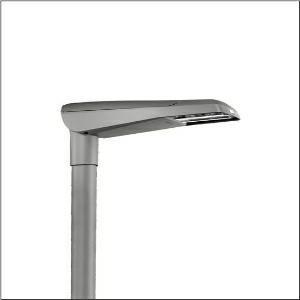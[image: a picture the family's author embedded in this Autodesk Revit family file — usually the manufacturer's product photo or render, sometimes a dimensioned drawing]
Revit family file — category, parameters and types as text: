
# Revit family: streetlight_sl_11_iq_micro___st1_2a_5xc1a51e08ce_3341
name_source: partatom
category: Lighting Fixtures
units: mm (PartAtom-declared; Revit-internal decimal feet)

## family parameters
Cut with Voids When Loaded = No
Host = Face
Light Source = No
Part Type = Normal
Room Calculation Point = No
Round Connector Dimension = Use Diameter
Shared = No

## types (1)
- --- (1 x LED, 1880 lm, 12.6 W, 3000K)
    Apparent Load = 13 VA
    CIE Flux Codes = 33 71 96 100 100
    Color Rendering = 70
    Color Temperature = 3000K
    Default Elevation = 1800 mm
    Description = Streetlight SL 11 iQ micro, mast luminaire, primary light control with 3 zone facetted reflector, of plastic, silver coated, highly specular, primary optical cover: cover, of PMMA, transparent, light distribution: ST1.2a, light emission: direct distribution, primary light characteristic: asymmetric, installation type: post-top, side-entry, lamps: LED, High Power LED, rated values: 1.880lm | 12,6W | 149,2lm/W (begin service life); end service life: 1.880lm | 12,9W; at 50% lumin. flux: 940lm | 6,8W | 138,2lm/W, colour temperature: 3000K, colour rendering: CRI > 70, light colour: 730, light setting 1 begin service life: 100% | 1.880lm | 12,6W | 149,2lm/W | 3.000K, light setting 1 end service life: 12,9W, further light settings possible, control: optimised constant luminous flux control (CLO 2.0), Desk-Remote (wireless, voltage-free reading and setting of iQ features in the workshop via application-optimized NFC function/RFID function), Light-Fading, Smart-Wire, Night-Set, Lumen-Switch, Temp-Guard, Auto-Match, with cable H07RN-F 5x 1.5mm², mains connection: 230..240V, AC, 50/60Hz, connection cable pre-assembled, cable length: 5,5m, luminaire housing, of diecast aluminium, powder-coated, Siteco® metallic grey (DB 702S), please order mast flange separately, inclination adjustable without tools: 0°, 5°, 10°, 15° (post-top) | 0°, -5°, -10°, -15° (side-entry), sealing non-destructively replaceable, multi-level sealing system, length: 600mm, width: 174mm, height: 116mm, mast flange for spigot size: 42mm (side-entry): 5XC10008XM4, 60/48mm (side-entry/post-top): 5XC10108XM2, 76/60mm (side-entry/post-top): 5XC10108XM1, equipment: standard, protection rating (complete): IP66, insulation class (complete): insulation class II (safety insulation), certification: CE, ENEC, ENEC+, VDE, impact resistance: IK10, permissible operating ambient temperature for outdoor applications: -25..+50°C, standard-compliant lighting for roads and squares, Environmental Product Declaration (EPD) tested and certified by an independent institute, packaging unit: 1 piece

Light Distribution: ST1.2a
    Height = 116 mm
    Lamp = 1 x LED
    Lamp Light Flux = 1880 lm
    Lamp Power = 12.6 W
    Lamp count = 1
    Length = 600 mm
    Luminous efficacy = 149 lm/W
    Manufacturer = Siteco
    ModVariant = No
    Model = 5XC1A51E08CE
    Number of Poles = 1
    OnlyDefault = Yes
    Power Factor = 1
    Product Name = Streetlight SL 11 iQ micro | ST1.2a
    Product group = mast luminaire | pylon top
    ProductGroupID = 6100
    Protection Class = Protection class II
    Protection Degree = IP 66
    RLX_Detail_Level = 1
    RLX_Emergency_Light_Flux = 0 lm
    RLX_Emergency_Type = 0
    RLX_Emergency_Type_DB = No
    RlxData = <blob elided: 26541 chars, md5=8722cc43>
    Socket = socket
    Standby Power = 0 W
    System Light Flux = 1880 lm
    System Power = 13 W
    Type Comments = factory setting: luminous flux: 100 % | dim-lin: 254 | 229 mA
    Type Image = l_1006566.jpg
    URL = http://relux.com
    VarID = @adj_000993
    Voltage = 0 V
    Weight = 0.00 kg
    Width = 174 mm

## geometry (parser evidence)
native form markers: Blend x4, Sweep x10
no freeform markers — native parametric forms only
